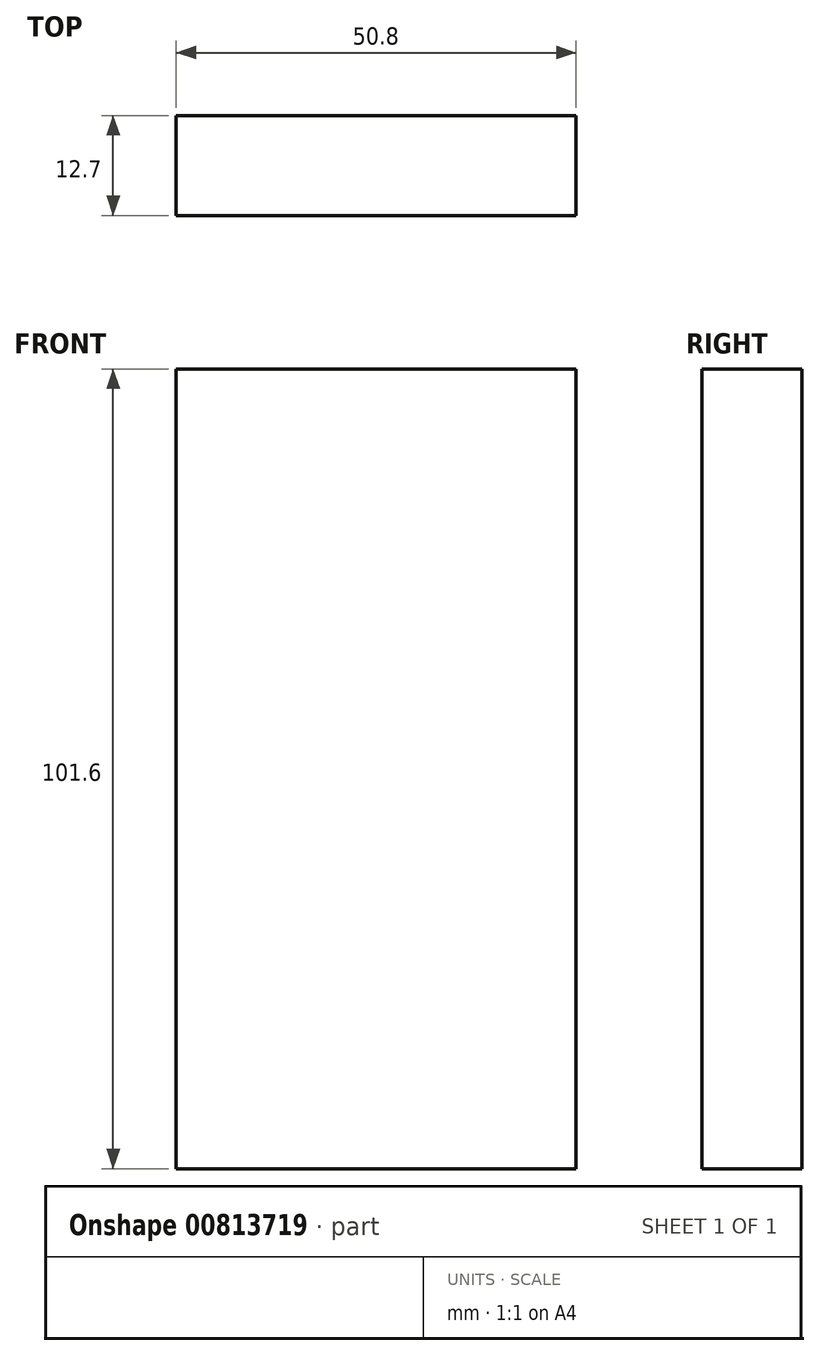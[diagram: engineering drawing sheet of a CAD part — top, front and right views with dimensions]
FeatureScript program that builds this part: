
annotation { "Feature Type Name" : "Feature", "Feature Type Description" : "" }
export const myFeature = defineFeature(function(context is Context, id is Id, definition is map)
    precondition{}
    {
        {
            var Q0;
            Q0=qCreatedBy(makeId("Front.planeOp"),FACE);
            var sketch = newSketch(context, id + "F0", { "sketchPlane" : qUnion([Q0])});
            skLineSegment(sketch, "E0.bottom", {"start": v(-25.4, 50.8) * mm, "end": v(25.4, 50.8) * mm});
            skLineSegment(sketch, "E0.top", {"start": v(-25.4, -50.8) * mm, "end": v(25.4, -50.8) * mm});
            skLineSegment(sketch, "E0.left", {"start": v(-25.4, 50.8) * mm, "end": v(-25.4, -50.8) * mm});
            skLineSegment(sketch, "E0.right", {"start": v(25.4, 50.8) * mm, "end": v(25.4, -50.8) * mm});
            skPoint(sketch, "E0.middle", {"position": v(0, 0) * mm});
            skSolve(sketch);
        }
        {
            var Q0;
            Q0 = qSketchRegion(id + "F0", true);
            extrude(context, id + "F1", {"entities" : qUnion([Q0]), "depth" : 12.7 * mm, "offsetDistance" : 25.4 * mm});
        }
    });
